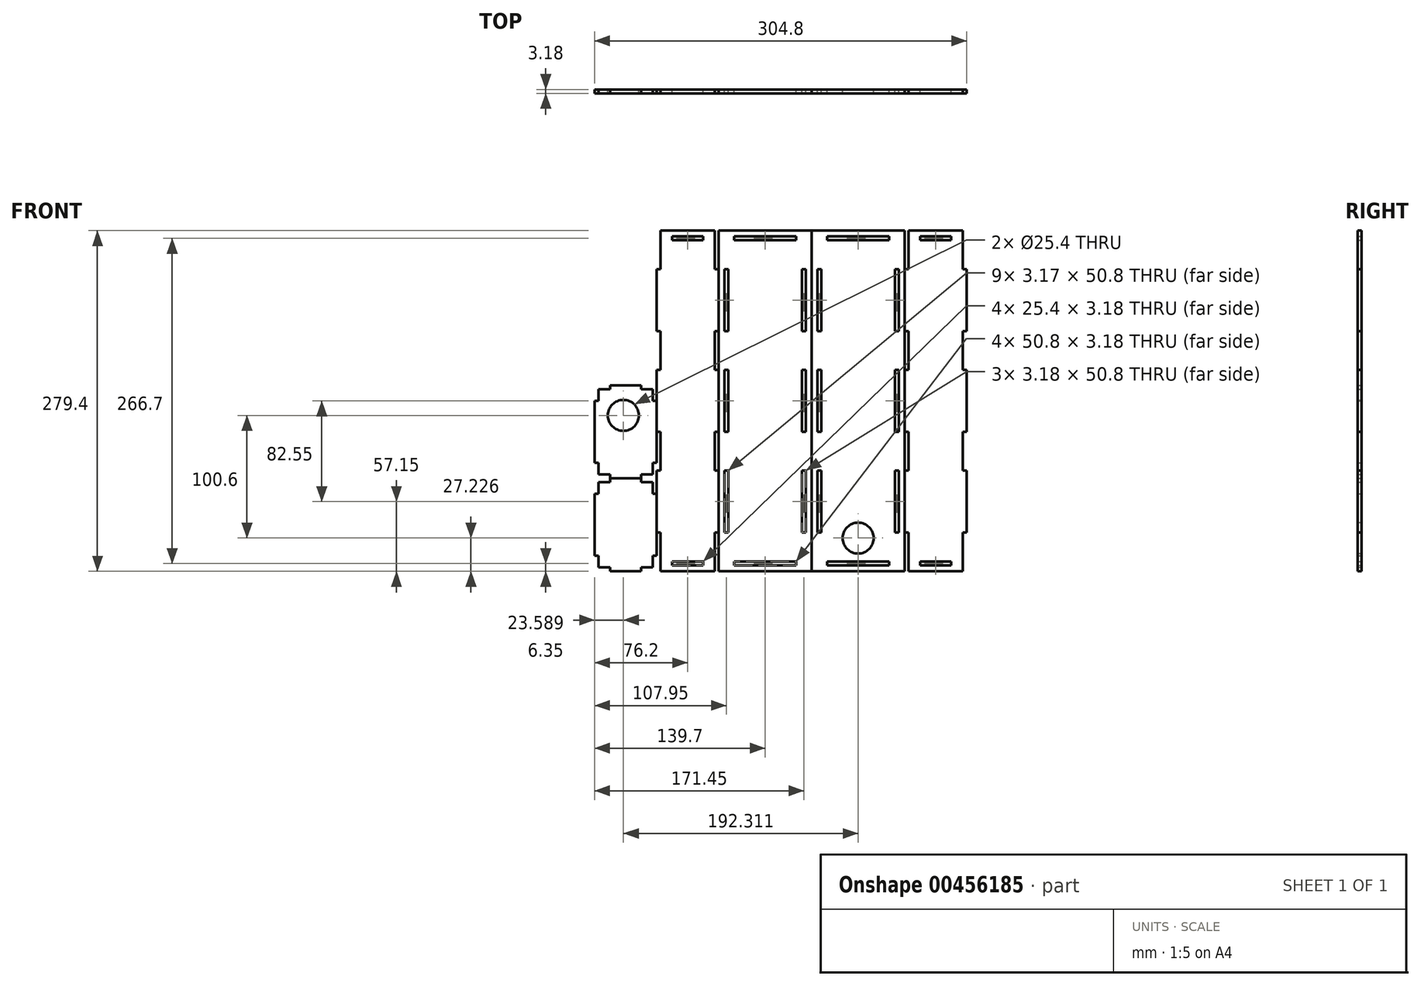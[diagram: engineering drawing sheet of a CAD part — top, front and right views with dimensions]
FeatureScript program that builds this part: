
annotation { "Feature Type Name" : "Feature", "Feature Type Description" : "" }
export const myFeature = defineFeature(function(context is Context, id is Id, definition is map)
    precondition{}
    {
        {
            var Q0;
            Q0=qCreatedBy(makeId("Front.planeOp"),FACE);
            var sketch = newSketch(context, id + "F0", { "sketchPlane" : qUnion([Q0])});
            skLineSegment(sketch, "E0.bottom", {"start": v(-38.1, 139.7) * mm, "end": v(38.1, 139.7) * mm});
            skLineSegment(sketch, "E0.top", {"start": v(-38.1, -139.7) * mm, "end": v(38.1, -139.7) * mm});
            skLineSegment(sketch, "E0.left", {"start": v(-38.1, 139.7) * mm, "end": v(-38.1, -139.7) * mm});
            skLineSegment(sketch, "E0.right", {"start": v(38.1, 139.7) * mm, "end": v(38.1, 107.95) * mm});
            skPoint(sketch, "E1", {"position": v(0, 0) * mm});
            skPoint(sketch, "E1.positionSnap0", {"position": v(0, 139.7) * mm});
            skPoint(sketch, "E1.positionSnap1", {"position": v(-38.1, 0) * mm});
            skLineSegment(sketch, "E2.bottom", {"start": v(-33.34, 107.95) * mm, "end": v(-30.16, 107.95) * mm});
            skLineSegment(sketch, "E2.top", {"start": v(-33.34, 57.15) * mm, "end": v(-30.16, 57.15) * mm});
            skLineSegment(sketch, "E2.left", {"start": v(-33.34, 107.95) * mm, "end": v(-33.34, 57.15) * mm});
            skLineSegment(sketch, "E2.right", {"start": v(-30.16, 107.95) * mm, "end": v(-30.16, 57.15) * mm});
            skLineSegment(sketch, "E3.bottom", {"start": v(-33.34, 25.4) * mm, "end": v(-30.16, 25.4) * mm});
            skLineSegment(sketch, "E3.top", {"start": v(-33.34, -25.4) * mm, "end": v(-30.16, -25.4) * mm});
            skLineSegment(sketch, "E3.left", {"start": v(-33.34, 25.4) * mm, "end": v(-33.34, -25.4) * mm});
            skLineSegment(sketch, "E3.right", {"start": v(-30.16, 25.4) * mm, "end": v(-30.16, -25.4) * mm});
            skLineSegment(sketch, "E4.bottom", {"start": v(-33.34, -57.15) * mm, "end": v(-30.16, -57.15) * mm});
            skLineSegment(sketch, "E4.top", {"start": v(-33.34, -107.95) * mm, "end": v(-30.16, -107.95) * mm});
            skLineSegment(sketch, "E4.left", {"start": v(-33.34, -57.15) * mm, "end": v(-33.34, -107.95) * mm});
            skLineSegment(sketch, "E4.right", {"start": v(-30.16, -57.15) * mm, "end": v(-30.16, -107.95) * mm});
            skLineSegment(sketch, "E5.bottom", {"start": v(30.16, 107.95) * mm, "end": v(33.34, 107.95) * mm});
            skLineSegment(sketch, "E5.top", {"start": v(30.16, 57.15) * mm, "end": v(33.34, 57.15) * mm});
            skLineSegment(sketch, "E5.left", {"start": v(30.16, 107.95) * mm, "end": v(30.16, 57.15) * mm});
            skLineSegment(sketch, "E5.right", {"start": v(33.34, 107.95) * mm, "end": v(33.34, 57.15) * mm});
            skLineSegment(sketch, "E6.bottom", {"start": v(30.16, 25.4) * mm, "end": v(33.34, 25.4) * mm});
            skLineSegment(sketch, "E6.top", {"start": v(30.16, -25.4) * mm, "end": v(33.34, -25.4) * mm});
            skLineSegment(sketch, "E6.left", {"start": v(30.16, 25.4) * mm, "end": v(30.16, -25.4) * mm});
            skLineSegment(sketch, "E6.right", {"start": v(33.34, 25.4) * mm, "end": v(33.34, -25.4) * mm});
            skLineSegment(sketch, "E7.bottom", {"start": v(30.16, -57.15) * mm, "end": v(33.34, -57.15) * mm});
            skLineSegment(sketch, "E7.top", {"start": v(30.16, -107.95) * mm, "end": v(33.34, -107.95) * mm});
            skLineSegment(sketch, "E7.left", {"start": v(30.16, -57.15) * mm, "end": v(30.16, -107.95) * mm});
            skLineSegment(sketch, "E7.right", {"start": v(33.34, -57.15) * mm, "end": v(33.34, -107.95) * mm});
            skLineSegment(sketch, "E8.bottom", {"start": v(-38.1, 139.7) * mm, "end": v(-114.3, 139.7) * mm});
            skLineSegment(sketch, "E8.top", {"start": v(-38.1, -139.7) * mm, "end": v(-114.3, -139.7) * mm});
            skLineSegment(sketch, "E8.right", {"start": v(-114.3, 139.7) * mm, "end": v(-114.3, -139.7) * mm});
            skLineSegment(sketch, "E9.bottom", {"start": v(-42.86, 107.95) * mm, "end": v(-46.04, 107.95) * mm});
            skLineSegment(sketch, "E9.top", {"start": v(-42.86, 57.15) * mm, "end": v(-46.04, 57.15) * mm});
            skLineSegment(sketch, "E9.left", {"start": v(-42.86, 107.95) * mm, "end": v(-42.86, 57.15) * mm});
            skLineSegment(sketch, "E9.right", {"start": v(-46.04, 107.95) * mm, "end": v(-46.04, 57.15) * mm});
            skLineSegment(sketch, "E10.bottom", {"start": v(-42.86, 25.4) * mm, "end": v(-46.04, 25.4) * mm});
            skLineSegment(sketch, "E10.top", {"start": v(-42.86, -25.4) * mm, "end": v(-46.04, -25.4) * mm});
            skLineSegment(sketch, "E10.left", {"start": v(-42.86, 25.4) * mm, "end": v(-42.86, -25.4) * mm});
            skLineSegment(sketch, "E10.right", {"start": v(-46.04, 25.4) * mm, "end": v(-46.04, -25.4) * mm});
            skLineSegment(sketch, "E11.bottom", {"start": v(-42.86, -57.15) * mm, "end": v(-46.04, -57.15) * mm});
            skLineSegment(sketch, "E11.top", {"start": v(-42.86, -107.95) * mm, "end": v(-46.04, -107.95) * mm});
            skLineSegment(sketch, "E11.left", {"start": v(-42.86, -57.15) * mm, "end": v(-42.86, -107.95) * mm});
            skLineSegment(sketch, "E11.right", {"start": v(-46.04, -57.15) * mm, "end": v(-46.04, -107.95) * mm});
            skLineSegment(sketch, "E12.bottom", {"start": v(-106.36, -107.95) * mm, "end": v(-109.54, -107.95) * mm});
            skLineSegment(sketch, "E12.top", {"start": v(-106.36, -57.15) * mm, "end": v(-109.54, -57.15) * mm});
            skLineSegment(sketch, "E12.left", {"start": v(-106.36, -107.95) * mm, "end": v(-106.36, -57.15) * mm});
            skLineSegment(sketch, "E12.right", {"start": v(-109.54, -107.95) * mm, "end": v(-109.54, -57.15) * mm});
            skLineSegment(sketch, "E13.bottom", {"start": v(-109.54, -25.4) * mm, "end": v(-106.36, -25.4) * mm});
            skLineSegment(sketch, "E13.top", {"start": v(-109.54, 25.4) * mm, "end": v(-106.36, 25.4) * mm});
            skLineSegment(sketch, "E13.left", {"start": v(-109.54, -25.4) * mm, "end": v(-109.54, 25.4) * mm});
            skLineSegment(sketch, "E13.right", {"start": v(-106.36, -25.4) * mm, "end": v(-106.36, 25.4) * mm});
            skLineSegment(sketch, "E14.bottom", {"start": v(-106.36, 57.15) * mm, "end": v(-109.54, 57.15) * mm});
            skLineSegment(sketch, "E14.top", {"start": v(-106.36, 107.95) * mm, "end": v(-109.54, 107.95) * mm});
            skLineSegment(sketch, "E14.left", {"start": v(-106.36, 57.15) * mm, "end": v(-106.36, 107.95) * mm});
            skLineSegment(sketch, "E14.right", {"start": v(-109.54, 57.15) * mm, "end": v(-109.54, 107.95) * mm});
            skLineSegment(sketch, "E15.left", {"start": v(38.1, 139.7) * mm, "end": v(38.1, -139.7) * mm});
            skLineSegment(sketch, "E15.right", {"start": v(88.9, 107.95) * mm, "end": v(88.9, 57.15) * mm});
            skLineSegment(sketch, "E16.bottom", {"start": v(38.1, 107.95) * mm, "end": v(41.27, 107.95) * mm});
            skLineSegment(sketch, "E16.top", {"start": v(38.1, 57.15) * mm, "end": v(41.27, 57.15) * mm});
            skLineSegment(sketch, "E16.left", {"start": v(38.1, 107.95) * mm, "end": v(38.1, 57.15) * mm});
            skLineSegment(sketch, "E17.bottom", {"start": v(38.1, 25.4) * mm, "end": v(41.28, 25.4) * mm});
            skLineSegment(sketch, "E17.top", {"start": v(38.1, -25.4) * mm, "end": v(41.28, -25.4) * mm});
            skLineSegment(sketch, "E17.left", {"start": v(38.1, 25.4) * mm, "end": v(38.1, -25.4) * mm});
            skLineSegment(sketch, "E18.bottom", {"start": v(38.1, -57.15) * mm, "end": v(41.28, -57.15) * mm});
            skLineSegment(sketch, "E18.top", {"start": v(38.1, -107.95) * mm, "end": v(41.28, -107.95) * mm});
            skLineSegment(sketch, "E18.left", {"start": v(38.1, -57.15) * mm, "end": v(38.1, -107.95) * mm});
            skLineSegment(sketch, "E19.bottom", {"start": v(88.9, 107.95) * mm, "end": v(85.73, 107.95) * mm});
            skLineSegment(sketch, "E19.top", {"start": v(88.9, 57.15) * mm, "end": v(85.73, 57.15) * mm});
            skLineSegment(sketch, "E20.bottom", {"start": v(88.9, 25.4) * mm, "end": v(85.73, 25.4) * mm});
            skLineSegment(sketch, "E20.top", {"start": v(88.9, -25.4) * mm, "end": v(85.73, -25.4) * mm});
            skLineSegment(sketch, "E20.left", {"start": v(88.9, 25.4) * mm, "end": v(88.9, -25.4) * mm});
            skLineSegment(sketch, "E21.bottom", {"start": v(88.9, -57.15) * mm, "end": v(85.73, -57.15) * mm});
            skLineSegment(sketch, "E21.top", {"start": v(88.9, -107.95) * mm, "end": v(85.73, -107.95) * mm});
            skLineSegment(sketch, "E21.left", {"start": v(88.9, -57.15) * mm, "end": v(88.9, -107.95) * mm});
            skLineSegment(sketch, "E22", {"start": v(41.27, 134.94) * mm, "end": v(41.27, 107.95) * mm});
            skLineSegment(sketch, "E23", {"start": v(85.73, 134.94) * mm, "end": v(85.73, 107.95) * mm});
            skLineSegment(sketch, "E24.trimOffspring", {"start": v(41.27, 57.15) * mm, "end": v(41.27, 25.4) * mm});
            skLineSegment(sketch, "E25.trimOffspring", {"start": v(85.73, 57.15) * mm, "end": v(85.73, 25.4) * mm});
            skLineSegment(sketch, "E26.trimOffspring", {"start": v(85.73, -25.4) * mm, "end": v(85.73, -57.15) * mm});
            skLineSegment(sketch, "E27.trimOffspring", {"start": v(85.73, -107.95) * mm, "end": v(85.73, -134.94) * mm});
            skLineSegment(sketch, "E28.trimOffspring", {"start": v(41.27, -107.95) * mm, "end": v(41.27, -134.94) * mm});
            skLineSegment(sketch, "E29.trimOffspring", {"start": v(41.27, -25.4) * mm, "end": v(41.27, -57.15) * mm});
            skPoint(sketch, "E30.orphan", {"position": v(88.9, -139.7) * mm});
            skLineSegment(sketch, "E31.left", {"start": v(-114.3, -139.7) * mm, "end": v(-114.3, 139.7) * mm});
            skLineSegment(sketch, "E31.right", {"start": v(-165.1, -107.95) * mm, "end": v(-165.1, -57.15) * mm});
            skLineSegment(sketch, "E32.bottom", {"start": v(-114.3, 107.95) * mm, "end": v(-117.47, 107.95) * mm});
            skLineSegment(sketch, "E32.right", {"start": v(-117.47, 107.95) * mm, "end": v(-117.47, 134.94) * mm});
            skLineSegment(sketch, "E33.bottom", {"start": v(-165.1, 107.95) * mm, "end": v(-161.93, 107.95) * mm});
            skLineSegment(sketch, "E33.right", {"start": v(-161.93, 107.95) * mm, "end": v(-161.93, 134.94) * mm});
            skLineSegment(sketch, "E34.bottom", {"start": v(-114.3, 25.4) * mm, "end": v(-117.47, 25.4) * mm});
            skLineSegment(sketch, "E34.top", {"start": v(-114.3, 57.15) * mm, "end": v(-117.47, 57.15) * mm});
            skLineSegment(sketch, "E34.left", {"start": v(-114.3, 25.4) * mm, "end": v(-114.3, 57.15) * mm});
            skLineSegment(sketch, "E34.right", {"start": v(-117.47, 25.4) * mm, "end": v(-117.47, 57.15) * mm});
            skLineSegment(sketch, "E35.bottom", {"start": v(-114.3, -25.4) * mm, "end": v(-117.47, -25.4) * mm});
            skLineSegment(sketch, "E35.top", {"start": v(-114.3, -57.15) * mm, "end": v(-117.47, -57.15) * mm});
            skLineSegment(sketch, "E35.right", {"start": v(-117.47, -25.4) * mm, "end": v(-117.47, -57.15) * mm});
            skLineSegment(sketch, "E36.bottom", {"start": v(-114.3, -107.95) * mm, "end": v(-117.47, -107.95) * mm});
            skLineSegment(sketch, "E36.left", {"start": v(-114.3, -107.95) * mm, "end": v(-114.3, -139.7) * mm});
            skLineSegment(sketch, "E36.right", {"start": v(-117.47, -107.95) * mm, "end": v(-117.47, -134.94) * mm});
            skLineSegment(sketch, "E37.bottom", {"start": v(-165.1, 57.15) * mm, "end": v(-161.93, 57.15) * mm});
            skLineSegment(sketch, "E37.top", {"start": v(-165.1, 25.4) * mm, "end": v(-161.93, 25.4) * mm});
            skLineSegment(sketch, "E37.right", {"start": v(-161.93, 57.15) * mm, "end": v(-161.93, 25.4) * mm});
            skLineSegment(sketch, "E38.bottom", {"start": v(-161.92, -25.4) * mm, "end": v(-165.1, -25.4) * mm});
            skLineSegment(sketch, "E38.top", {"start": v(-161.92, -57.15) * mm, "end": v(-165.1, -57.15) * mm});
            skLineSegment(sketch, "E38.left", {"start": v(-161.92, -25.4) * mm, "end": v(-161.92, -57.15) * mm});
            skLineSegment(sketch, "E39.top", {"start": v(-165.1, -107.95) * mm, "end": v(-161.93, -107.95) * mm});
            skLineSegment(sketch, "E39.right", {"start": v(-161.93, -134.94) * mm, "end": v(-161.93, -107.95) * mm});
            skPoint(sketch, "E40.orphan", {"position": v(-165.1, 139.7) * mm});
            skLineSegment(sketch, "E41.trimOffspring", {"start": v(-165.1, 57.15) * mm, "end": v(-165.1, 107.95) * mm});
            skLineSegment(sketch, "E42.trimOffspring", {"start": v(-165.1, -25.4) * mm, "end": v(-165.1, 25.4) * mm});
            skPoint(sketch, "E32.left.end.orphan", {"position": v(-114.3, 139.7) * mm});
            skLineSegment(sketch, "E43.bottom", {"start": v(-101.6, 134.94) * mm, "end": v(-50.8, 134.94) * mm});
            skLineSegment(sketch, "E43.top", {"start": v(-101.6, 131.76) * mm, "end": v(-50.8, 131.76) * mm});
            skLineSegment(sketch, "E43.left", {"start": v(-101.6, 134.94) * mm, "end": v(-101.6, 131.76) * mm});
            skLineSegment(sketch, "E43.right", {"start": v(-50.8, 134.94) * mm, "end": v(-50.8, 131.76) * mm});
            skLineSegment(sketch, "E44.bottom", {"start": v(-25.4, 131.76) * mm, "end": v(25.4, 131.76) * mm});
            skLineSegment(sketch, "E44.top", {"start": v(-25.4, 134.94) * mm, "end": v(25.4, 134.94) * mm});
            skLineSegment(sketch, "E44.left", {"start": v(-25.4, 131.76) * mm, "end": v(-25.4, 134.94) * mm});
            skLineSegment(sketch, "E44.right", {"start": v(25.4, 131.76) * mm, "end": v(25.4, 134.94) * mm});
            skLineSegment(sketch, "E45.bottom", {"start": v(-101.6, -134.94) * mm, "end": v(-50.8, -134.94) * mm});
            skLineSegment(sketch, "E45.top", {"start": v(-101.6, -131.76) * mm, "end": v(-50.8, -131.76) * mm});
            skLineSegment(sketch, "E45.left", {"start": v(-101.6, -134.94) * mm, "end": v(-101.6, -131.76) * mm});
            skLineSegment(sketch, "E45.right", {"start": v(-50.8, -134.94) * mm, "end": v(-50.8, -131.76) * mm});
            skLineSegment(sketch, "E46.bottom", {"start": v(-25.4, -134.94) * mm, "end": v(25.4, -134.94) * mm});
            skLineSegment(sketch, "E46.top", {"start": v(-25.4, -131.76) * mm, "end": v(25.4, -131.76) * mm});
            skLineSegment(sketch, "E46.left", {"start": v(-25.4, -134.94) * mm, "end": v(-25.4, -131.76) * mm});
            skLineSegment(sketch, "E46.right", {"start": v(25.4, -134.94) * mm, "end": v(25.4, -131.76) * mm});
            skPoint(sketch, "E47.orphan", {"position": v(-161.93, 139.7) * mm});
            skPoint(sketch, "E48.orphan", {"position": v(-117.47, 139.7) * mm});
            skPoint(sketch, "E49.orphan", {"position": v(-117.47, -139.7) * mm});
            skPoint(sketch, "E50.orphan", {"position": v(85.73, 139.7) * mm});
            skPoint(sketch, "E51.orphan", {"position": v(41.27, 139.7) * mm});
            skCircle(sketch, "E52", {"center": v(0, -112.47) * mm, "radius": 12.7 * mm});
            skLineSegment(sketch, "E53.left", {"start": v(-165.1, -107.95) * mm, "end": v(-165.1, -58.74) * mm});
            skLineSegment(sketch, "E54.top", {"start": v(-117.47, 139.7) * mm, "end": v(-161.93, 139.7) * mm});
            skLineSegment(sketch, "E54.left", {"start": v(-117.47, 134.94) * mm, "end": v(-117.47, 139.7) * mm});
            skLineSegment(sketch, "E54.right", {"start": v(-161.93, 134.94) * mm, "end": v(-161.93, 139.7) * mm});
            skLineSegment(sketch, "E55.top", {"start": v(-161.93, -139.7) * mm, "end": v(-117.47, -139.7) * mm});
            skLineSegment(sketch, "E55.left", {"start": v(-161.93, -134.94) * mm, "end": v(-161.93, -139.7) * mm});
            skLineSegment(sketch, "E55.right", {"start": v(-117.47, -134.94) * mm, "end": v(-117.47, -139.7) * mm});
            skLineSegment(sketch, "E56.top", {"start": v(41.27, -139.7) * mm, "end": v(85.73, -139.7) * mm});
            skLineSegment(sketch, "E56.left", {"start": v(41.27, -134.94) * mm, "end": v(41.27, -139.7) * mm});
            skLineSegment(sketch, "E56.right", {"start": v(85.73, -134.94) * mm, "end": v(85.73, -139.7) * mm});
            skLineSegment(sketch, "E57.top", {"start": v(41.27, 139.7) * mm, "end": v(85.73, 139.7) * mm});
            skLineSegment(sketch, "E57.left", {"start": v(41.27, 134.94) * mm, "end": v(41.27, 139.7) * mm});
            skLineSegment(sketch, "E57.right", {"start": v(85.73, 134.94) * mm, "end": v(85.73, 139.7) * mm});
            skLineSegment(sketch, "E58.bottom", {"start": v(-127, 131.76) * mm, "end": v(-152.4, 131.76) * mm});
            skLineSegment(sketch, "E58.top", {"start": v(-127, 134.94) * mm, "end": v(-152.4, 134.94) * mm});
            skLineSegment(sketch, "E58.left", {"start": v(-127, 131.76) * mm, "end": v(-127, 134.94) * mm});
            skLineSegment(sketch, "E58.right", {"start": v(-152.4, 131.76) * mm, "end": v(-152.4, 134.94) * mm});
            skLineSegment(sketch, "E59.bottom", {"start": v(50.8, 131.76) * mm, "end": v(76.2, 131.76) * mm});
            skLineSegment(sketch, "E59.top", {"start": v(50.8, 134.94) * mm, "end": v(76.2, 134.94) * mm});
            skLineSegment(sketch, "E59.left", {"start": v(50.8, 131.76) * mm, "end": v(50.8, 134.94) * mm});
            skLineSegment(sketch, "E59.right", {"start": v(76.2, 131.76) * mm, "end": v(76.2, 134.94) * mm});
            skPoint(sketch, "E60.right.end.orphan", {"position": v(-168.27, -66.67) * mm});
            skPoint(sketch, "E60.left.end.orphan", {"position": v(-212.72, -66.67) * mm});
            skPoint(sketch, "E60.left.start.orphan", {"position": v(-212.72, -63.5) * mm});
            skPoint(sketch, "E61.orphan", {"position": v(-165.1, -134.94) * mm});
            skPoint(sketch, "E62.left.start.orphan", {"position": v(-168.27, -130.18) * mm});
            skPoint(sketch, "E62.right.end.orphan", {"position": v(-212.72, -127) * mm});
            skPoint(sketch, "E62.right.start.orphan", {"position": v(-212.72, -130.18) * mm});
            skLineSegment(sketch, "E63.bottom", {"start": v(-152.4, -134.94) * mm, "end": v(-127, -134.94) * mm});
            skLineSegment(sketch, "E63.top", {"start": v(-152.4, -131.76) * mm, "end": v(-127, -131.76) * mm});
            skLineSegment(sketch, "E63.left", {"start": v(-152.4, -134.94) * mm, "end": v(-152.4, -131.76) * mm});
            skLineSegment(sketch, "E63.right", {"start": v(-127, -134.94) * mm, "end": v(-127, -131.76) * mm});
            skLineSegment(sketch, "E64.bottom", {"start": v(50.8, -134.94) * mm, "end": v(76.2, -134.94) * mm});
            skLineSegment(sketch, "E64.top", {"start": v(50.8, -131.76) * mm, "end": v(76.2, -131.76) * mm});
            skLineSegment(sketch, "E64.left", {"start": v(50.8, -134.94) * mm, "end": v(50.8, -131.76) * mm});
            skLineSegment(sketch, "E64.right", {"start": v(76.2, -134.94) * mm, "end": v(76.2, -131.76) * mm});
            skLineSegment(sketch, "E65.bottom", {"start": v(-177.8, -139.7) * mm, "end": v(-203.2, -139.7) * mm});
            skLineSegment(sketch, "E66.bottom", {"start": v(-203.2, -63.5) * mm, "end": v(-177.8, -63.5) * mm});
            skLineSegment(sketch, "E66.left", {"start": v(-203.2, -63.5) * mm, "end": v(-203.2, -66.67) * mm});
            skLineSegment(sketch, "E66.right", {"start": v(-177.8, -63.5) * mm, "end": v(-177.8, -66.67) * mm});
            skLineSegment(sketch, "E67.bottom", {"start": v(-203.2, -139.7) * mm, "end": v(-177.8, -139.7) * mm});
            skLineSegment(sketch, "E67.left", {"start": v(-203.2, -139.7) * mm, "end": v(-203.2, -136.53) * mm});
            skLineSegment(sketch, "E67.right", {"start": v(-177.8, -139.7) * mm, "end": v(-177.8, -136.53) * mm});
            skLineSegment(sketch, "E68.bottom", {"start": v(-215.9, -76.2) * mm, "end": v(-212.72, -76.2) * mm});
            skLineSegment(sketch, "E68.top", {"start": v(-215.9, -127) * mm, "end": v(-212.72, -127) * mm});
            skLineSegment(sketch, "E68.left", {"start": v(-215.9, -76.2) * mm, "end": v(-215.9, -127) * mm});
            skLineSegment(sketch, "E69.bottom", {"start": v(-165.1, -127) * mm, "end": v(-168.28, -127) * mm});
            skLineSegment(sketch, "E69.top", {"start": v(-165.1, -76.2) * mm, "end": v(-168.27, -76.2) * mm});
            skLineSegment(sketch, "E69.left", {"start": v(-165.1, -127) * mm, "end": v(-165.1, -76.2) * mm});
            skLineSegment(sketch, "E70", {"start": v(-212.72, -66.67) * mm, "end": v(-212.72, -76.2) * mm});
            skLineSegment(sketch, "E71", {"start": v(-168.27, -66.67) * mm, "end": v(-168.27, -76.2) * mm});
            skPoint(sketch, "E71.startSnap0", {"position": v(-190.5, -63.5) * mm});
            skLineSegment(sketch, "E72", {"start": v(-212.72, -66.67) * mm, "end": v(-203.2, -66.67) * mm});
            skLineSegment(sketch, "E73", {"start": v(-212.72, -136.53) * mm, "end": v(-203.2, -136.53) * mm});
            skLineSegment(sketch, "E74.trimOffspring", {"start": v(-177.8, -63.5) * mm, "end": v(-203.2, -63.5) * mm});
            skPoint(sketch, "E65.top.end.orphan", {"position": v(-168.27, -63.5) * mm});
            skPoint(sketch, "E75.orphan", {"position": v(-215.9, -63.5) * mm});
            skPoint(sketch, "E76.orphan", {"position": v(-215.9, -66.67) * mm});
            skLineSegment(sketch, "E77.trimOffspring", {"start": v(-215.9, -127) * mm, "end": v(-215.9, -76.2) * mm});
            skPoint(sketch, "E65.right.end.orphan", {"position": v(-215.9, -136.53) * mm});
            skLineSegment(sketch, "E78.trimOffspring", {"start": v(-165.1, -127) * mm, "end": v(-165.1, -63.5) * mm});
            skPoint(sketch, "E79.orphan", {"position": v(-165.1, -139.7) * mm});
            skLineSegment(sketch, "E80.trimOffspring", {"start": v(-212.72, -127) * mm, "end": v(-212.72, -136.53) * mm});
            skLineSegment(sketch, "E81.trimOffspring", {"start": v(-168.27, -127) * mm, "end": v(-168.27, -136.53) * mm});
            skLineSegment(sketch, "E82.trimOffspring", {"start": v(-177.8, -136.53) * mm, "end": v(-168.27, -136.53) * mm});
            skLineSegment(sketch, "E83.trimOffspring", {"start": v(-177.8, -66.67) * mm, "end": v(-168.27, -66.67) * mm});
            skLineSegment(sketch, "E84.bottom", {"start": v(-177.66, -63.5) * mm, "end": v(-203.06, -63.5) * mm});
            skLineSegment(sketch, "E85.bottom", {"start": v(-203.06, 12.7) * mm, "end": v(-177.66, 12.7) * mm});
            skLineSegment(sketch, "E85.left", {"start": v(-203.06, 12.7) * mm, "end": v(-203.06, 9.53) * mm});
            skLineSegment(sketch, "E85.right", {"start": v(-177.66, 12.7) * mm, "end": v(-177.66, 9.53) * mm});
            skLineSegment(sketch, "E86.left", {"start": v(-203.06, -63.5) * mm, "end": v(-203.06, -60.32) * mm});
            skLineSegment(sketch, "E86.right", {"start": v(-177.66, -63.5) * mm, "end": v(-177.66, -60.32) * mm});
            skLineSegment(sketch, "E87.bottom", {"start": v(-215.76, 0) * mm, "end": v(-212.59, 0) * mm});
            skLineSegment(sketch, "E87.top", {"start": v(-215.76, -50.8) * mm, "end": v(-212.59, -50.8) * mm});
            skLineSegment(sketch, "E88.bottom", {"start": v(-164.96, -50.8) * mm, "end": v(-168.14, -50.8) * mm});
            skLineSegment(sketch, "E88.top", {"start": v(-164.96, 0) * mm, "end": v(-168.14, 0) * mm});
            skLineSegment(sketch, "E88.left", {"start": v(-164.96, -50.8) * mm, "end": v(-164.96, 0) * mm});
            skLineSegment(sketch, "E89", {"start": v(-212.59, 9.53) * mm, "end": v(-212.59, 0) * mm});
            skLineSegment(sketch, "E90", {"start": v(-168.14, 9.53) * mm, "end": v(-168.14, 0) * mm});
            skLineSegment(sketch, "E91", {"start": v(-212.59, 9.53) * mm, "end": v(-203.06, 9.53) * mm});
            skLineSegment(sketch, "E92", {"start": v(-212.59, -60.32) * mm, "end": v(-203.06, -60.32) * mm});
            skLineSegment(sketch, "E93.trimOffspring", {"start": v(-215.76, -50.8) * mm, "end": v(-215.76, 0) * mm});
            skLineSegment(sketch, "E94.trimOffspring", {"start": v(-212.59, -50.8) * mm, "end": v(-212.59, -60.32) * mm});
            skLineSegment(sketch, "E95.trimOffspring", {"start": v(-168.14, -50.8) * mm, "end": v(-168.14, -60.32) * mm});
            skLineSegment(sketch, "E96.trimOffspring", {"start": v(-177.66, -60.32) * mm, "end": v(-168.14, -60.32) * mm});
            skLineSegment(sketch, "E97.trimOffspring", {"start": v(-177.66, 9.53) * mm, "end": v(-168.14, 9.53) * mm});
            skCircle(sketch, "E98", {"center": v(-192.31, -11.87) * mm, "radius": 12.7 * mm});
            skSolve(sketch);
        }
        {
            var Q0;
            Q0=makeQuery(id+"F0.imprint","IMPRINT",FACE,{"disambiguationData":[TD([[makeQuery(id+"F0.imprint","IMPRINT",EDGE,{"derivedFrom":sQuery(id+"F0.wireOp",EDGE,"E8.bottom")}),1.0]])]});
            extrude(context, id + "F1", {"entities" : qUnion([Q0]), "depth" : 3.17 * mm});
        }
        {
            var Q0;
            Q0=makeQuery(id+"F0.imprint","IMPRINT",FACE,{"disambiguationData":[TD([[makeQuery(id+"F0.imprint","IMPRINT",EDGE,{"derivedFrom":sQuery(id+"F0.wireOp",EDGE,"E0.bottom")}),-1.0]])]});
            extrude(context, id + "F2", {"entities" : qUnion([Q0]), "depth" : 3.17 * mm});
        }
        {
            var Q0;
            Q0=makeQuery(id+"F0.imprint","IMPRINT",FACE,{"disambiguationData":[TD([[makeQuery(id+"F0.imprint","IMPRINT",EDGE,{"derivedFrom":sQuery(id+"F0.wireOp",EDGE,"E16.bottom")}),-1.0]])]});
            extrude(context, id + "F3", {"entities" : qUnion([Q0]), "depth" : 3.17 * mm});
        }
        {
            var Q0;
            Q0=makeQuery(id+"F0.imprint","IMPRINT",FACE,{"disambiguationData":[TD([[makeQuery(id+"F0.imprint","IMPRINT",EDGE,{"derivedFrom":sQuery(id+"F0.wireOp",EDGE,"E31.right")}),-1.0]])]});
            extrude(context, id + "F4", {"entities" : qUnion([Q0]), "depth" : 3.17 * mm});
        }
        {
            var Q0;
            Q0=makeQuery(id+"F0.imprint","IMPRINT",FACE,{"disambiguationData":[TD([[makeQuery(id+"F0.imprint","IMPRINT",EDGE,{"derivedFrom":sQuery(id+"F0.wireOp",EDGE,"E85.bottom")}),-1.0]])]});
            extrude(context, id + "F5", {"entities" : qUnion([Q0]), "depth" : 3.17 * mm});
        }
        {
            var Q0;
            Q0=makeQuery(id+"F0.imprint","IMPRINT",FACE,{"disambiguationData":[TD([[makeQuery(id+"F0.imprint","IMPRINT",EDGE,{"derivedFrom":sQuery(id+"F0.wireOp",EDGE,"E66.left")}),1.0]])]});
            extrude(context, id + "F6", {"entities" : qUnion([Q0]), "depth" : 3.17 * mm});
        }
    });
